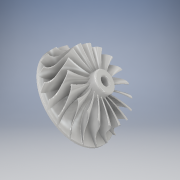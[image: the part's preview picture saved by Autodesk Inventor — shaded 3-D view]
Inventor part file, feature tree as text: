
AUTODESK INVENTOR PART (.ipt)
format: ipt  version: 2018.2 (Build 222227000, 227)  size: 3,265,024 bytes
history: native  units: in
note: dims shown in document units (in); Inventor stores cm internally (conversion verified against a paired STEP export)
features: other x36, loft x36, fillet x22, sketch x7, plane x3, revolve x2, pattern_circular x2, thicken_offset x1
ambient origin geometry x8: Origin, YZ Plane, XZ Plane, XY Plane, X Axis, Y Axis, Z Axis, Center Point
bodies: Solid1 (feature_tree)
feature tree (109):
  sketch  "Sketch1"  dims[d0=20.0in d1=4.2in]
  plane  "Work Plane1"
  sketch  "Sketch2"  dims[d2=6.0in d3=50.0in d4=30.5in]
  sketch  "Sketch3"  dims[d5=10.0in]
  plane  "Work Plane2"
  sketch  "Sketch4"  dims[d6=15.0in]
  plane  "Work Plane3"
  thicken_offset  "Thicken1"
  revolve  "Revolution1"  [1 undecoded]
  revolve  "Revolution2"  [1 undecoded]
  fillet  "Fillet1"  Radius=30.5in
  pattern_circular  "Circular Pattern1"  Count=127  [1 undecoded]
  pattern_circular  "Circular Pattern2"  Angle=90.0deg  [1 undecoded]
  fillet  "Fillet2"  [1 undecoded]
  fillet  "Fillet3"  Radius=0.65in
  fillet  "Fillet4"  Radius=0.65in
  fillet  "Fillet5"  Radius=8.0in
  fillet  "Fillet6"  Radius=3.0in
  fillet  "Fillet7"  Radius=24.5in
  fillet  "Fillet8"  Radius=30.5in
  fillet  "Fillet9"  Radius=1.8in
  fillet  "Fillet10"  [1 undecoded]
  fillet  "Fillet11"  Radius=20.0in
  fillet  "Fillet12"  [1 undecoded]
  fillet  "Fillet13"  Radius=4.0in
  fillet  "Fillet14"  Radius=20.0in
  fillet  "Fillet15"  [1 undecoded]
  fillet  "Fillet16"  Radius=5.0in
  fillet  "Fillet17"  [1 undecoded]
  fillet  "Fillet18"  Radius=0.3in
  fillet  "Fillet19"  Radius=0.7874in
  fillet  "Fillet20"  Radius=7.0866in
  fillet  "Fillet21"  Radius=1.0in
  fillet  "Fillet22"  Radius=1.0in
  sketch  "Sketch5"  dims[d7=20.0in d8=50.0in]
  other  "Srf1"
  sketch  "Sketch6"  dims[d9=0.0in d10=90.0deg]
  sketch  "Sketch7"  dims[d11=0.0in d12=90.0deg d13=0.0in d14=90.0deg d15=0.0in d16=90.0deg d17=0.65in d18=0.65in d19=8.0in d20=3.0in d21=24.5in d22=30.5in d23=1.8in d24=90.0deg d25=20.0in d26=90.0deg d27=4.0in d28=20.0in d29=90.0deg d30=5.0in d31=90.0deg d32=0.3in d33=0.7874in d34=360.0deg d36=7.0866in d37=360.0deg d39=1.0in d40=1.0in d41=1.0in d42=0.3in d43=0.3in d44=0.3in d45=0.3in d46=0.3in d47=0.3in d48=0.3in d49=0.3in d50=0.3in d51=0.3in d52=0.3in d53=0.3in d54=0.3in d55=0.3in d56=0.3in d57=0.3in d58=0.3in d59=0.3in]
  other  "Srf2"
  other  "Srf4"
  other  "Srf6"
  other  "Srf8"
  other  "Srf10"
  other  "Srf12"
  other  "Srf14"
  other  "Srf16"
  other  "Srf18"
  other  "Srf20"
  other  "Srf22"
  other  "Srf24"
  other  "Srf26"
  other  "Srf28"
  other  "Srf30"
  other  "Srf32"
  other  "Srf34"
  other  "Srf36"
  other  "Srf3"
  other  "Srf5"
  other  "Srf7"
  other  "Srf9"
  other  "Srf11"
  other  "Srf13"
  other  "Srf15"
  other  "Srf17"
  other  "Srf19"
  other  "Srf21"
  other  "Srf23"
  other  "Srf25"
  other  "Srf27"
  other  "Srf29"
  other  "Srf31"
  other  "Srf33"
  other  "Srf35"
  loft  "LoftSrf1"
  loft  "LoftSrf2"
  loft  "LoftSrf3"
  loft  "LoftSrf4"
  loft  "LoftSrf5"
  loft  "LoftSrf6"
  loft  "LoftSrf7"
  loft  "LoftSrf8"
  loft  "LoftSrf9"
  loft  "LoftSrf10"
  loft  "LoftSrf11"
  loft  "LoftSrf12"
  loft  "LoftSrf13"
  loft  "LoftSrf14"
  loft  "LoftSrf15"
  loft  "LoftSrf16"
  loft  "LoftSrf17"
  loft  "LoftSrf18"
  loft  "LoftSrf19"
  loft  "LoftSrf20"
  loft  "LoftSrf21"
  loft  "LoftSrf22"
  loft  "LoftSrf23"
  loft  "LoftSrf24"
  loft  "LoftSrf25"
  loft  "LoftSrf26"
  loft  "LoftSrf27"
  loft  "LoftSrf28"
  loft  "LoftSrf29"
  loft  "LoftSrf30"
  loft  "LoftSrf31"
  loft  "LoftSrf32"
  loft  "LoftSrf33"
  loft  "LoftSrf34"
  loft  "LoftSrf35"
  loft  "LoftSrf36"
note: 9 required parameter values undecoded (feature->parameter linkage not recoverable at this tier; creation-order binding heuristic only, values carry confidence <= 0.55)